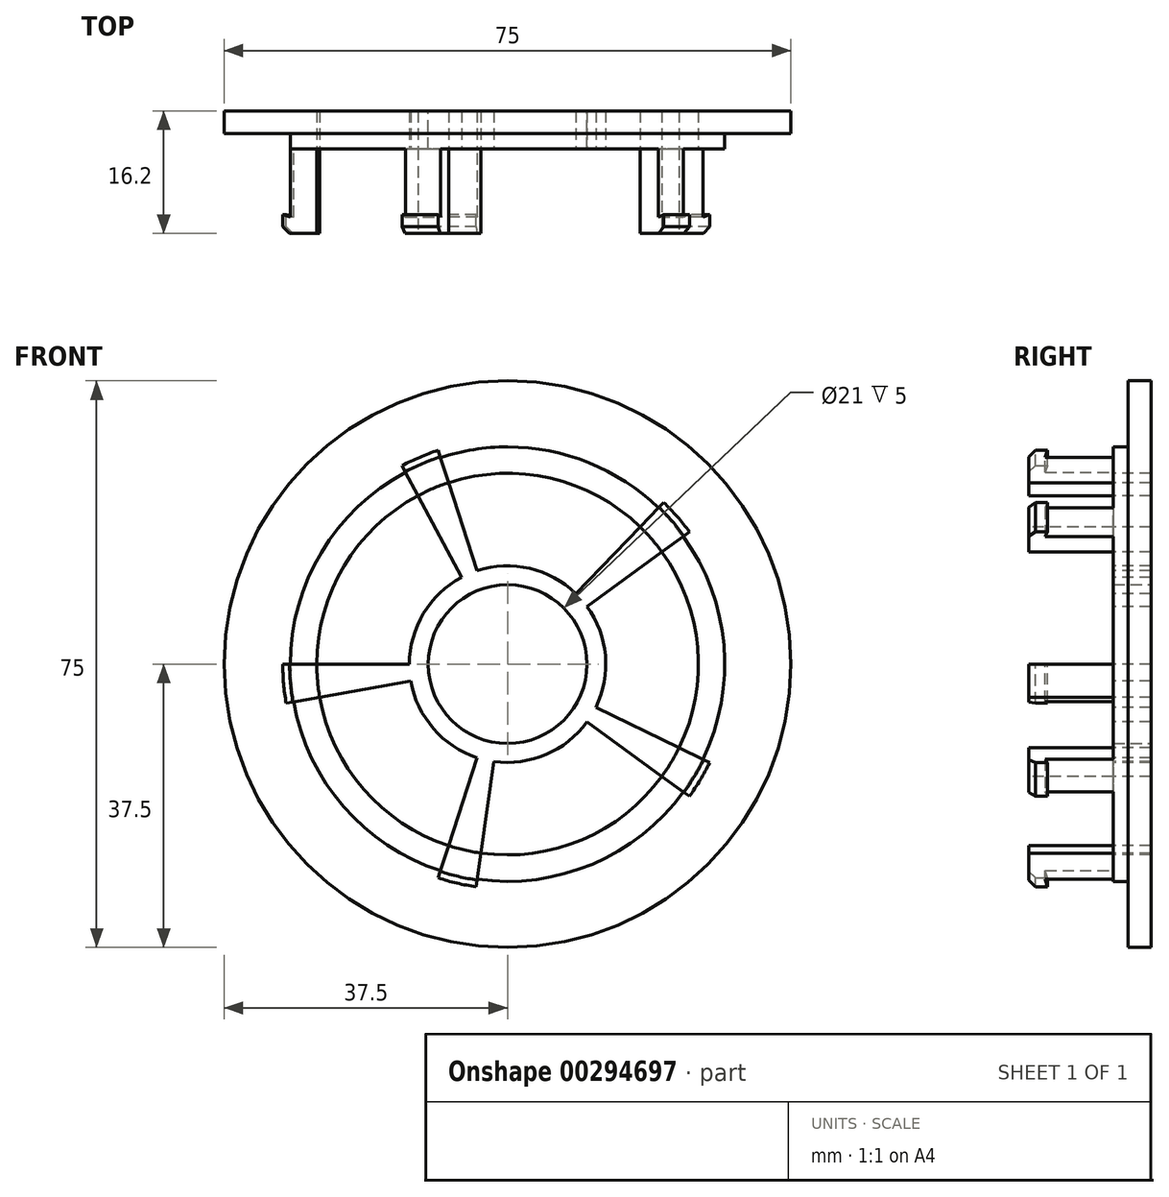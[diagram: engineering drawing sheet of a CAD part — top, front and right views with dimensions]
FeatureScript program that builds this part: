
annotation { "Feature Type Name" : "Feature", "Feature Type Description" : "" }
export const myFeature = defineFeature(function(context is Context, id is Id, definition is map)
    precondition{}
    {
        {
            var Q0;
            Q0=qCreatedBy(makeId("Front.planeOp"),FACE);
            var sketch = newSketch(context, id + "F0", { "sketchPlane" : qUnion([Q0])});
            skCircle(sketch, "E0", {"center": v(0, 0) * mm, "radius": 37.5 * mm});
            skCircle(sketch, "E1", {"center": v(0, 0) * mm, "radius": 10.5 * mm});
            skCircle(sketch, "E2", {"center": v(0, 0) * mm, "radius": 28.75 * mm});
            skSolve(sketch);
        }
        {
            var Q0;
            Q0=makeQuery(id+"F0.imprint","IMPRINT",FACE,{"disambiguationData":[TD([[makeQuery(id+"F0.imprint","IMPRINT",EDGE,{"derivedFrom":sQuery(id+"F0.wireOp",EDGE,"E0")}),1.0]])]});
            var Q1;
            Q1=makeQuery(id+"F0.imprint","IMPRINT",FACE,{"disambiguationData":[TD([[makeQuery(id+"F0.imprint","IMPRINT",EDGE,{"derivedFrom":sQuery(id+"F0.wireOp",EDGE,"E1")}),-1.0]])]});
            var Q2;
            Q2=sQuery(id+"F0.wireOp",EDGE,"E0");
            var Q3;
            Q3=sQuery(id+"F0.wireOp",EDGE,"E2");
            extrude(context, id + "F1", {"entities" : qUnion([Q0, Q1]), "surfaceEntities" : qUnion([Q2, Q3]), "depth" : 3 * mm});
        }
        {
            var Q0;
            Q0=qCreatedBy(makeId("Top.planeOp"),FACE);
            var sketch = newSketch(context, id + "F2", { "sketchPlane" : qUnion([Q0])});
            skLineSegment(sketch, "E3", {"start": v(-25.25, -3) * mm, "end": v(-25.25, -16.2) * mm});
            skLineSegment(sketch, "E4", {"start": v(-29.75, -16.2) * mm, "end": v(-29.75, -13.7) * mm});
            skLineSegment(sketch, "E5", {"start": v(-29.75, -13.7) * mm, "end": v(-28.75, -14) * mm});
            skLineSegment(sketch, "E6", {"start": v(-28.75, -14) * mm, "end": v(-28.75, -3) * mm});
            skLineSegment(sketch, "E7", {"start": v(-28.75, -3) * mm, "end": v(-25.25, -3) * mm});
            skLineSegment(sketch, "E8", {"start": v(-25.25, -16.2) * mm, "end": v(-29.75, -16.2) * mm});
            skSolve(sketch);
        }
        {
            var Q0;
            Q0 = qSketchRegion(id + "F2", true);
            var Q1;
            Q1=sQuery(id+"F0.wireOp",EDGE,"E2");
            revolve(context, id + "F3", {"operationType" : NewBodyOperationType.ADD, "entities" : qUnion([Q0]), "axis" : qUnion([Q1]), "revolveType" : RevolveType.ONE_DIRECTION, "angle" : 10 * degree});
        }
        {
            var Q0;
            Q0=makeQuery(id+"F1.opExtrude","SWEPT_BODY",BODY,{"disambiguationData":[OSD([sQuery(id+"F0.wireOp",EDGE,"E0"),sQuery(id+"F0.wireOp",EDGE,"E1")])]});
            var Q1;
            Q1=sQuery(id+"F0.wireOp",EDGE,"E2");
            circularPattern(context, id + "F4", {"operationType" : NewBodyOperationType.ADD, "entities" : qUnion([Q0]), "axis" : qUnion([Q1]), "angle" : 360 * degree, "instanceCount" : 5, "equalSpace" : true});
        }
        {
            var Q0;
            Q0=makeQuery(id+"F0.imprint","IMPRINT",FACE,{"disambiguationData":[TD([[makeQuery(id+"F0.imprint","IMPRINT",EDGE,{"derivedFrom":sQuery(id+"F0.wireOp",EDGE,"E1")}),-1.0]])]});
            extrude(context, id + "F5", {"entities" : qUnion([Q0]), "operationType" : NewBodyOperationType.ADD, "depth" : 5 * mm});
        }
        {
            var Q0;
            Q0=makeQuery(id+"F3.opRevolve","SWEPT_EDGE",EDGE,{"disambiguationData":[OSD([sQuery(id+"F2.wireOp",EDGE,"E4"),sQuery(id+"F2.wireOp",EDGE,"E8")])]});
            var Q1;
            Q1=makeQuery(id+"F4.opPattern","COPY",EDGE,{"derivedFrom":makeQuery(id+"F3.opRevolve","SWEPT_EDGE",EDGE,{"disambiguationData":[OSD([sQuery(id+"F2.wireOp",EDGE,"E4"),sQuery(id+"F2.wireOp",EDGE,"E8")])]}),"instanceName":"1"});
            var Q2;
            Q2=makeQuery(id+"F4.opPattern","COPY",EDGE,{"derivedFrom":makeQuery(id+"F3.opRevolve","SWEPT_EDGE",EDGE,{"disambiguationData":[OSD([sQuery(id+"F2.wireOp",EDGE,"E4"),sQuery(id+"F2.wireOp",EDGE,"E8")])]}),"instanceName":"2"});
            var Q3;
            Q3=makeQuery(id+"F4.opPattern","COPY",EDGE,{"derivedFrom":makeQuery(id+"F3.opRevolve","SWEPT_EDGE",EDGE,{"disambiguationData":[OSD([sQuery(id+"F2.wireOp",EDGE,"E4"),sQuery(id+"F2.wireOp",EDGE,"E8")])]}),"instanceName":"3"});
            var Q4;
            Q4=makeQuery(id+"F4.opPattern","COPY",EDGE,{"derivedFrom":makeQuery(id+"F3.opRevolve","SWEPT_EDGE",EDGE,{"disambiguationData":[OSD([sQuery(id+"F2.wireOp",EDGE,"E4"),sQuery(id+"F2.wireOp",EDGE,"E8")])]}),"instanceName":"4"});
            var Q5;
            Q5=makeQuery(id+"F4.opPattern","COPY",EDGE,{"derivedFrom":makeQuery(id+"F3.opRevolve","SWEPT_EDGE",EDGE,{"disambiguationData":[OSD([sQuery(id+"F2.wireOp",EDGE,"E4"),sQuery(id+"F2.wireOp",EDGE,"E8")])]}),"instanceName":"5"});
            var Q6;
            Q6=makeQuery(id+"F4.opPattern","COPY",EDGE,{"derivedFrom":makeQuery(id+"F3.opRevolve","SWEPT_EDGE",EDGE,{"disambiguationData":[OSD([sQuery(id+"F2.wireOp",EDGE,"E4"),sQuery(id+"F2.wireOp",EDGE,"E8")])]}),"instanceName":"6"});
            var Q7;
            Q7=makeQuery(id+"F4.opPattern","COPY",EDGE,{"derivedFrom":makeQuery(id+"F3.opRevolve","SWEPT_EDGE",EDGE,{"disambiguationData":[OSD([sQuery(id+"F2.wireOp",EDGE,"E4"),sQuery(id+"F2.wireOp",EDGE,"E8")])]}),"instanceName":"7"});
            chamfer(context, id + "F6", {"entities" : qUnion([Q0, Q1, Q2, Q3, Q4, Q5, Q6, Q7]), "width" : 0.9 * mm, "tangentPropagation" : true});
        }
        {
            var Q0;
            Q0=makeQuery(id+"F5.opExtrude","CAP_FACE",FACE,{"disambiguationData":[OSD([sQuery(id+"F0.wireOp",EDGE,"E1"),sQuery(id+"F0.wireOp",EDGE,"E2")])],"isStart":false});
            var sketch = newSketch(context, id + "F7", { "sketchPlane" : qUnion([Q0])});
            skCircle(sketch, "E9", {"center": v(0, 0) * mm, "radius": 13 * mm});
            skLineSegment(sketch, "E10", {"start": v(-13.5, 25.38) * mm, "end": v(-6.1, 11.48) * mm});
            skLineSegment(sketch, "E11", {"start": v(-8.88, 27.34) * mm, "end": v(-4.02, 12.36) * mm});
            skCircle(sketch, "E12", {"center": v(0, 0) * mm, "radius": 25.25 * mm});
            skLineSegment(sketch, "E13", {"start": v(-28.75, 0) * mm, "end": v(-13, 0) * mm});
            skLineSegment(sketch, "E14", {"start": v(-28.31, -5) * mm, "end": v(-12.8, -2.26) * mm});
            skLineSegment(sketch, "E15", {"start": v(-8.88, -27.34) * mm, "end": v(-4.02, -12.36) * mm});
            skLineSegment(sketch, "E16", {"start": v(-4, -28.47) * mm, "end": v(-1.8, -12.87) * mm});
            skLineSegment(sketch, "E17", {"start": v(23.26, -16.9) * mm, "end": v(10.52, -7.64) * mm});
            skLineSegment(sketch, "E18", {"start": v(25.84, -12.6) * mm, "end": v(11.68, -5.7) * mm});
            skLineSegment(sketch, "E19", {"start": v(23.26, 16.9) * mm, "end": v(10.52, 7.64) * mm});
            skLineSegment(sketch, "E20", {"start": v(19.97, 20.68) * mm, "end": v(9.03, 9.35) * mm});
            skSolve(sketch);
        }
        {
            var Q0;
            {var subQ0=sQuery(id+"F7.wireOp",EDGE,"E10");var subQ1=sQuery(id+"F7.wireOp",EDGE,"E9");var subQ2=makeQuery(id+"F7.imprint","INTERSECT",VERTEX,{"derivedFrom":[subQ1,subQ0]});Q0=makeQuery(id+"F7.imprint","IMPRINT",FACE,{"disambiguationData":[TD([[makeQuery(id+"F7.imprint","IMPRINT",EDGE,{"disambiguationData":[TD([[subQ2,-1.0]])],"derivedFrom":subQ1}),-1.0]])]});}
            var Q1;
            {var subQ0=sQuery(id+"F7.wireOp",EDGE,"E14");var subQ1=sQuery(id+"F7.wireOp",EDGE,"E9");var subQ2=makeQuery(id+"F7.imprint","INTERSECT",VERTEX,{"derivedFrom":[subQ1,subQ0]});Q1=makeQuery(id+"F7.imprint","IMPRINT",FACE,{"disambiguationData":[TD([[makeQuery(id+"F7.imprint","IMPRINT",EDGE,{"disambiguationData":[TD([[subQ2,-1.0]])],"derivedFrom":subQ1}),-1.0]])]});}
            var Q2;
            {var subQ0=sQuery(id+"F7.wireOp",EDGE,"E16");var subQ1=sQuery(id+"F7.wireOp",EDGE,"E9");var subQ2=makeQuery(id+"F7.imprint","INTERSECT",VERTEX,{"derivedFrom":[subQ1,subQ0]});Q2=makeQuery(id+"F7.imprint","IMPRINT",FACE,{"disambiguationData":[TD([[makeQuery(id+"F7.imprint","IMPRINT",EDGE,{"disambiguationData":[TD([[subQ2,-1.0]])],"derivedFrom":subQ1}),-1.0]])]});}
            var Q3;
            {var subQ0=sQuery(id+"F7.wireOp",EDGE,"E19");var subQ1=sQuery(id+"F7.wireOp",EDGE,"E9");var subQ2=makeQuery(id+"F7.imprint","INTERSECT",VERTEX,{"derivedFrom":[subQ1,subQ0]});Q3=makeQuery(id+"F7.imprint","IMPRINT",FACE,{"disambiguationData":[TD([[makeQuery(id+"F7.imprint","IMPRINT",EDGE,{"disambiguationData":[TD([[subQ2,1.0]])],"derivedFrom":subQ1}),-1.0]])]});}
            var Q4;
            {var subQ0=sQuery(id+"F7.wireOp",EDGE,"E20");var subQ1=sQuery(id+"F7.wireOp",EDGE,"E9");var subQ2=makeQuery(id+"F7.imprint","INTERSECT",VERTEX,{"derivedFrom":[subQ1,subQ0]});Q4=makeQuery(id+"F7.imprint","IMPRINT",FACE,{"disambiguationData":[TD([[makeQuery(id+"F7.imprint","IMPRINT",EDGE,{"disambiguationData":[TD([[subQ2,-1.0]])],"derivedFrom":subQ1}),-1.0]])]});}
            extrude(context, id + "F8", {"entities" : qUnion([Q0, Q1, Q2, Q3, Q4]), "operationType" : NewBodyOperationType.REMOVE, "oppositeDirection" : true, "depth" : 25 * mm});
        }
    });
